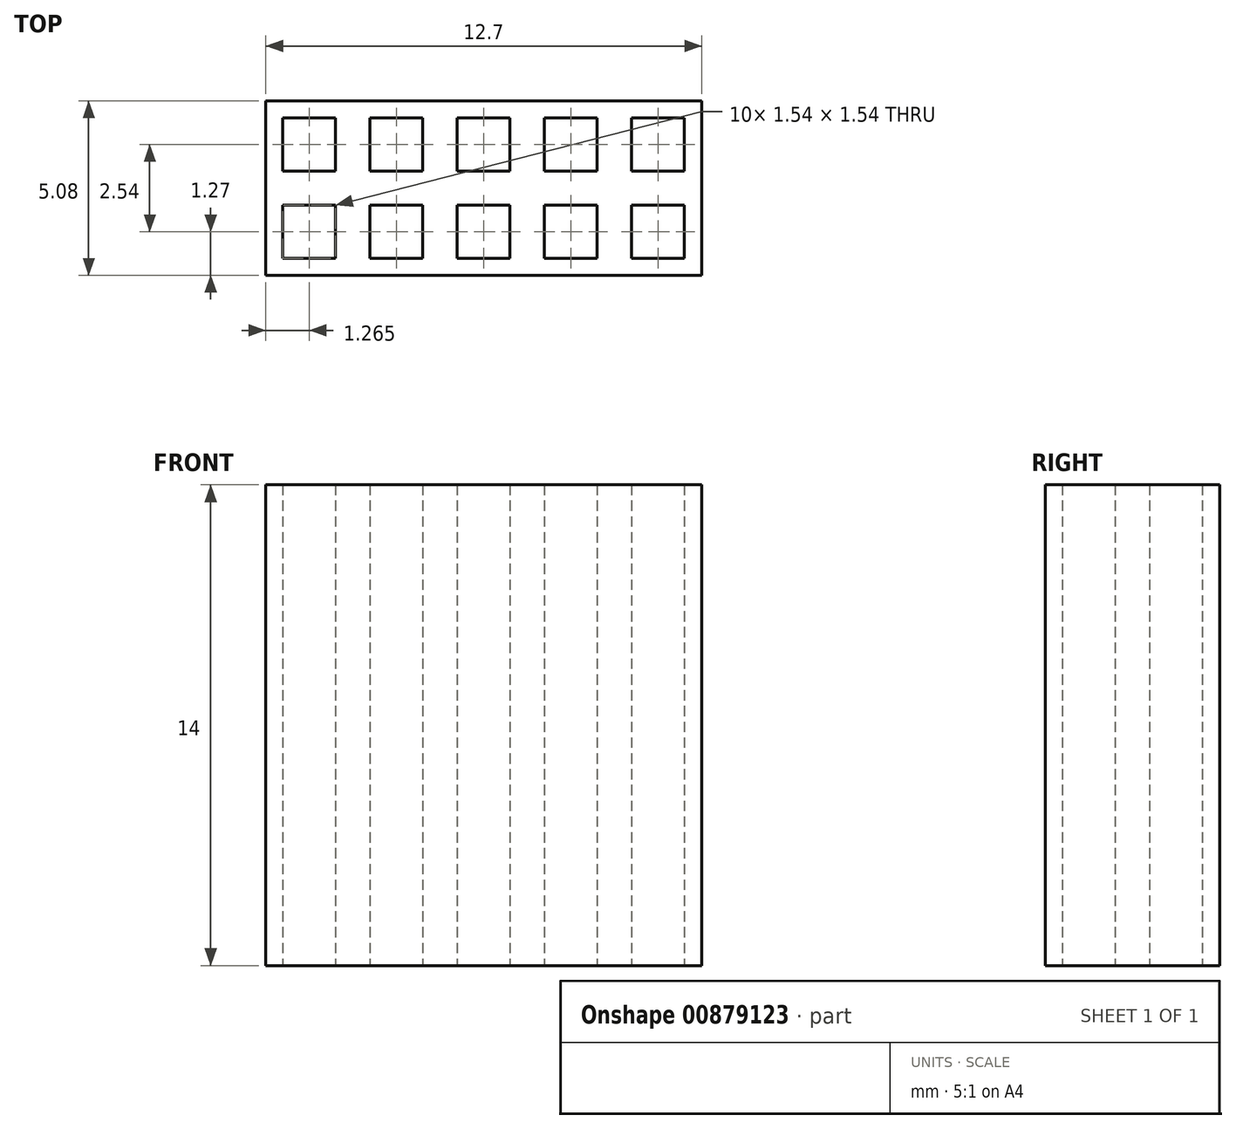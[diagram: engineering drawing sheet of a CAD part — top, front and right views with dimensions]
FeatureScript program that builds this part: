
annotation { "Feature Type Name" : "Feature", "Feature Type Description" : "" }
export const myFeature = defineFeature(function(context is Context, id is Id, definition is map)
    precondition{}
    {
        {
            var Q0;
            Q0=qCreatedBy(makeId("Top.planeOp"),FACE);
            var sketch = newSketch(context, id + "F0", { "sketchPlane" : qUnion([Q0])});
            skLineSegment(sketch, "E0.bottom", {"start": v(-36.65, 22.38) * mm, "end": v(-34.11, 22.38) * mm});
            skLineSegment(sketch, "E0.top", {"start": v(-36.65, 19.84) * mm, "end": v(-34.11, 19.84) * mm});
            skLineSegment(sketch, "E0.left", {"start": v(-36.65, 22.38) * mm, "end": v(-36.65, 19.84) * mm});
            skLineSegment(sketch, "E0.right", {"start": v(-34.11, 22.38) * mm, "end": v(-34.11, 19.84) * mm});
            skLineSegment(sketch, "E1.0", {"start": v(-36.15, 21.88) * mm, "end": v(-36.15, 20.34) * mm});
            skLineSegment(sketch, "E1.1", {"start": v(-36.15, 21.88) * mm, "end": v(-34.61, 21.88) * mm});
            skLineSegment(sketch, "E1.2", {"start": v(-34.61, 21.88) * mm, "end": v(-34.61, 20.34) * mm});
            skLineSegment(sketch, "E1.3", {"start": v(-36.15, 20.34) * mm, "end": v(-34.61, 20.34) * mm});
            skLineSegment(sketch, "E2.0.1.0", {"start": v(-34.11, 24.92) * mm, "end": v(-34.11, 22.38) * mm});
            skLineSegment(sketch, "E2.0.1.1", {"start": v(-36.65, 24.92) * mm, "end": v(-34.11, 24.92) * mm});
            skLineSegment(sketch, "E2.0.1.2", {"start": v(-36.15, 24.42) * mm, "end": v(-34.61, 24.42) * mm});
            skLineSegment(sketch, "E2.0.1.3", {"start": v(-36.15, 22.88) * mm, "end": v(-34.61, 22.88) * mm});
            skLineSegment(sketch, "E2.0.1.4", {"start": v(-34.61, 24.42) * mm, "end": v(-34.61, 22.88) * mm});
            skLineSegment(sketch, "E2.0.1.6", {"start": v(-36.15, 24.42) * mm, "end": v(-36.15, 22.88) * mm});
            skLineSegment(sketch, "E2.0.1.7", {"start": v(-36.65, 24.92) * mm, "end": v(-36.65, 22.38) * mm});
            skLineSegment(sketch, "E2.1.0.0", {"start": v(-31.57, 22.38) * mm, "end": v(-31.57, 19.84) * mm});
            skLineSegment(sketch, "E2.1.0.1", {"start": v(-34.11, 22.38) * mm, "end": v(-31.57, 22.38) * mm});
            skLineSegment(sketch, "E2.1.0.2", {"start": v(-33.61, 21.88) * mm, "end": v(-32.07, 21.88) * mm});
            skLineSegment(sketch, "E2.1.0.3", {"start": v(-33.61, 20.34) * mm, "end": v(-32.07, 20.34) * mm});
            skLineSegment(sketch, "E2.1.0.4", {"start": v(-32.07, 21.88) * mm, "end": v(-32.07, 20.34) * mm});
            skLineSegment(sketch, "E2.1.0.5", {"start": v(-34.11, 19.84) * mm, "end": v(-31.57, 19.84) * mm});
            skLineSegment(sketch, "E2.1.0.6", {"start": v(-33.61, 21.88) * mm, "end": v(-33.61, 20.34) * mm});
            skLineSegment(sketch, "E2.1.1.0", {"start": v(-31.57, 24.92) * mm, "end": v(-31.57, 22.38) * mm});
            skLineSegment(sketch, "E2.1.1.1", {"start": v(-34.11, 24.92) * mm, "end": v(-31.57, 24.92) * mm});
            skLineSegment(sketch, "E2.1.1.2", {"start": v(-33.61, 24.42) * mm, "end": v(-32.07, 24.42) * mm});
            skLineSegment(sketch, "E2.1.1.3", {"start": v(-33.61, 22.88) * mm, "end": v(-32.07, 22.88) * mm});
            skLineSegment(sketch, "E2.1.1.4", {"start": v(-32.07, 24.42) * mm, "end": v(-32.07, 22.88) * mm});
            skLineSegment(sketch, "E2.1.1.5", {"start": v(-34.11, 22.38) * mm, "end": v(-31.57, 22.38) * mm});
            skLineSegment(sketch, "E2.1.1.6", {"start": v(-33.61, 24.42) * mm, "end": v(-33.61, 22.88) * mm});
            skLineSegment(sketch, "E2.1.1.7", {"start": v(-34.11, 24.92) * mm, "end": v(-34.11, 22.38) * mm});
            skLineSegment(sketch, "E2.2.0.0", {"start": v(-29.03, 22.38) * mm, "end": v(-29.03, 19.84) * mm});
            skLineSegment(sketch, "E2.2.0.1", {"start": v(-31.57, 22.38) * mm, "end": v(-29.03, 22.38) * mm});
            skLineSegment(sketch, "E2.2.0.2", {"start": v(-31.07, 21.88) * mm, "end": v(-29.53, 21.88) * mm});
            skLineSegment(sketch, "E2.2.0.3", {"start": v(-31.07, 20.34) * mm, "end": v(-29.53, 20.34) * mm});
            skLineSegment(sketch, "E2.2.0.4", {"start": v(-29.53, 21.88) * mm, "end": v(-29.53, 20.34) * mm});
            skLineSegment(sketch, "E2.2.0.5", {"start": v(-31.57, 19.84) * mm, "end": v(-29.03, 19.84) * mm});
            skLineSegment(sketch, "E2.2.0.6", {"start": v(-31.07, 21.88) * mm, "end": v(-31.07, 20.34) * mm});
            skLineSegment(sketch, "E2.2.0.7", {"start": v(-31.57, 22.38) * mm, "end": v(-31.57, 19.84) * mm});
            skLineSegment(sketch, "E2.2.1.0", {"start": v(-29.03, 24.92) * mm, "end": v(-29.03, 22.38) * mm});
            skLineSegment(sketch, "E2.2.1.1", {"start": v(-31.57, 24.92) * mm, "end": v(-29.03, 24.92) * mm});
            skLineSegment(sketch, "E2.2.1.2", {"start": v(-31.07, 24.42) * mm, "end": v(-29.53, 24.42) * mm});
            skLineSegment(sketch, "E2.2.1.3", {"start": v(-31.07, 22.88) * mm, "end": v(-29.53, 22.88) * mm});
            skLineSegment(sketch, "E2.2.1.4", {"start": v(-29.53, 24.42) * mm, "end": v(-29.53, 22.88) * mm});
            skLineSegment(sketch, "E2.2.1.5", {"start": v(-31.57, 22.38) * mm, "end": v(-29.03, 22.38) * mm});
            skLineSegment(sketch, "E2.2.1.6", {"start": v(-31.07, 24.42) * mm, "end": v(-31.07, 22.88) * mm});
            skLineSegment(sketch, "E2.2.1.7", {"start": v(-31.57, 24.92) * mm, "end": v(-31.57, 22.38) * mm});
            skLineSegment(sketch, "E2.3.0.0", {"start": v(-26.5, 22.38) * mm, "end": v(-26.5, 19.84) * mm});
            skLineSegment(sketch, "E2.3.0.1", {"start": v(-29.03, 22.38) * mm, "end": v(-26.5, 22.38) * mm});
            skLineSegment(sketch, "E2.3.0.2", {"start": v(-28.53, 21.88) * mm, "end": v(-27, 21.88) * mm});
            skLineSegment(sketch, "E2.3.0.3", {"start": v(-28.53, 20.34) * mm, "end": v(-27, 20.34) * mm});
            skLineSegment(sketch, "E2.3.0.4", {"start": v(-27, 21.88) * mm, "end": v(-27, 20.34) * mm});
            skLineSegment(sketch, "E2.3.0.5", {"start": v(-29.03, 19.84) * mm, "end": v(-26.5, 19.84) * mm});
            skLineSegment(sketch, "E2.3.0.6", {"start": v(-28.53, 21.88) * mm, "end": v(-28.53, 20.34) * mm});
            skLineSegment(sketch, "E2.3.0.7", {"start": v(-29.03, 22.38) * mm, "end": v(-29.03, 19.84) * mm});
            skLineSegment(sketch, "E2.3.1.0", {"start": v(-26.5, 24.92) * mm, "end": v(-26.5, 22.38) * mm});
            skLineSegment(sketch, "E2.3.1.1", {"start": v(-29.03, 24.92) * mm, "end": v(-26.5, 24.92) * mm});
            skLineSegment(sketch, "E2.3.1.2", {"start": v(-28.53, 24.42) * mm, "end": v(-27, 24.42) * mm});
            skLineSegment(sketch, "E2.3.1.3", {"start": v(-28.53, 22.88) * mm, "end": v(-27, 22.88) * mm});
            skLineSegment(sketch, "E2.3.1.4", {"start": v(-27, 24.42) * mm, "end": v(-27, 22.88) * mm});
            skLineSegment(sketch, "E2.3.1.5", {"start": v(-29.03, 22.38) * mm, "end": v(-26.5, 22.38) * mm});
            skLineSegment(sketch, "E2.3.1.6", {"start": v(-28.53, 24.42) * mm, "end": v(-28.53, 22.88) * mm});
            skLineSegment(sketch, "E2.3.1.7", {"start": v(-29.03, 24.92) * mm, "end": v(-29.03, 22.38) * mm});
            skLineSegment(sketch, "E2.4.0.0", {"start": v(-23.95, 22.38) * mm, "end": v(-23.95, 19.84) * mm});
            skLineSegment(sketch, "E2.4.0.1", {"start": v(-26.5, 22.38) * mm, "end": v(-23.95, 22.38) * mm});
            skLineSegment(sketch, "E2.4.0.2", {"start": v(-26, 21.88) * mm, "end": v(-24.45, 21.88) * mm});
            skLineSegment(sketch, "E2.4.0.3", {"start": v(-26, 20.34) * mm, "end": v(-24.45, 20.34) * mm});
            skLineSegment(sketch, "E2.4.0.4", {"start": v(-24.45, 21.88) * mm, "end": v(-24.45, 20.34) * mm});
            skLineSegment(sketch, "E2.4.0.5", {"start": v(-26.5, 19.84) * mm, "end": v(-23.95, 19.84) * mm});
            skLineSegment(sketch, "E2.4.0.6", {"start": v(-26, 21.88) * mm, "end": v(-26, 20.34) * mm});
            skLineSegment(sketch, "E2.4.0.7", {"start": v(-26.5, 22.38) * mm, "end": v(-26.5, 19.84) * mm});
            skLineSegment(sketch, "E2.4.1.0", {"start": v(-23.95, 24.92) * mm, "end": v(-23.95, 22.38) * mm});
            skLineSegment(sketch, "E2.4.1.1", {"start": v(-26.5, 24.92) * mm, "end": v(-23.95, 24.92) * mm});
            skLineSegment(sketch, "E2.4.1.2", {"start": v(-26, 24.42) * mm, "end": v(-24.45, 24.42) * mm});
            skLineSegment(sketch, "E2.4.1.3", {"start": v(-26, 22.88) * mm, "end": v(-24.45, 22.88) * mm});
            skLineSegment(sketch, "E2.4.1.4", {"start": v(-24.45, 24.42) * mm, "end": v(-24.45, 22.88) * mm});
            skLineSegment(sketch, "E2.4.1.5", {"start": v(-26.5, 22.38) * mm, "end": v(-23.95, 22.38) * mm});
            skLineSegment(sketch, "E2.4.1.6", {"start": v(-26, 24.42) * mm, "end": v(-26, 22.88) * mm});
            skLineSegment(sketch, "E2.4.1.7", {"start": v(-26.5, 24.92) * mm, "end": v(-26.5, 22.38) * mm});
            skLineSegment(sketch, "E2.direction1", {"start": v(-36.65, 19.84) * mm, "end": v(-34.11, 19.84) * mm, "construction": true});
            skLineSegment(sketch, "E2.direction2", {"start": v(-36.65, 19.84) * mm, "end": v(-36.65, 22.38) * mm, "construction": true});
            skSolve(sketch);
        }
        {
            var Q0;
            Q0=makeQuery(id+"F0.imprint","IMPRINT",FACE,{"disambiguationData":[TD([[makeQuery(id+"F0.imprint","IMPRINT",EDGE,{"derivedFrom":sQuery(id+"F0.wireOp",EDGE,"E0.top")}),1.0]])]});
            var Q1;
            Q1=makeQuery(id+"F0.imprint","IMPRINT",FACE,{"disambiguationData":[TD([[makeQuery(id+"F0.imprint","IMPRINT",EDGE,{"derivedFrom":sQuery(id+"F0.wireOp",EDGE,"E2.0.1.1")}),-1.0]])]});
            var Q2;
            Q2=makeQuery(id+"F0.imprint","IMPRINT",FACE,{"disambiguationData":[TD([[makeQuery(id+"F0.imprint","IMPRINT",EDGE,{"derivedFrom":sQuery(id+"F0.wireOp",EDGE,"E2.1.1.1")}),-1.0]])]});
            var Q3;
            Q3=makeQuery(id+"F0.imprint","IMPRINT",FACE,{"disambiguationData":[TD([[makeQuery(id+"F0.imprint","IMPRINT",EDGE,{"derivedFrom":sQuery(id+"F0.wireOp",EDGE,"E2.1.0.2")}),1.0]])]});
            var Q4;
            Q4=makeQuery(id+"F0.imprint","IMPRINT",FACE,{"disambiguationData":[TD([[makeQuery(id+"F0.imprint","IMPRINT",EDGE,{"derivedFrom":sQuery(id+"F0.wireOp",EDGE,"E2.2.0.2")}),1.0]])]});
            var Q5;
            Q5=makeQuery(id+"F0.imprint","IMPRINT",FACE,{"disambiguationData":[TD([[makeQuery(id+"F0.imprint","IMPRINT",EDGE,{"derivedFrom":sQuery(id+"F0.wireOp",EDGE,"E2.2.1.1")}),-1.0]])]});
            var Q6;
            Q6=makeQuery(id+"F0.imprint","IMPRINT",FACE,{"disambiguationData":[TD([[makeQuery(id+"F0.imprint","IMPRINT",EDGE,{"derivedFrom":sQuery(id+"F0.wireOp",EDGE,"E2.3.1.1")}),-1.0]])]});
            var Q7;
            Q7=makeQuery(id+"F0.imprint","IMPRINT",FACE,{"disambiguationData":[TD([[makeQuery(id+"F0.imprint","IMPRINT",EDGE,{"derivedFrom":sQuery(id+"F0.wireOp",EDGE,"E2.3.0.2")}),1.0]])]});
            var Q8;
            Q8=makeQuery(id+"F0.imprint","IMPRINT",FACE,{"disambiguationData":[TD([[makeQuery(id+"F0.imprint","IMPRINT",EDGE,{"derivedFrom":sQuery(id+"F0.wireOp",EDGE,"E2.4.0.0")}),-1.0]])]});
            var Q9;
            Q9=makeQuery(id+"F0.imprint","IMPRINT",FACE,{"disambiguationData":[TD([[makeQuery(id+"F0.imprint","IMPRINT",EDGE,{"derivedFrom":sQuery(id+"F0.wireOp",EDGE,"E2.4.1.0")}),-1.0]])]});
            extrude(context, id + "F1", {"entities" : qUnion([Q0, Q1, Q2, Q3, Q4, Q5, Q6, Q7, Q8, Q9]), "depth" : 14 * mm, "offsetDistance" : 25 * mm});
        }
    });
